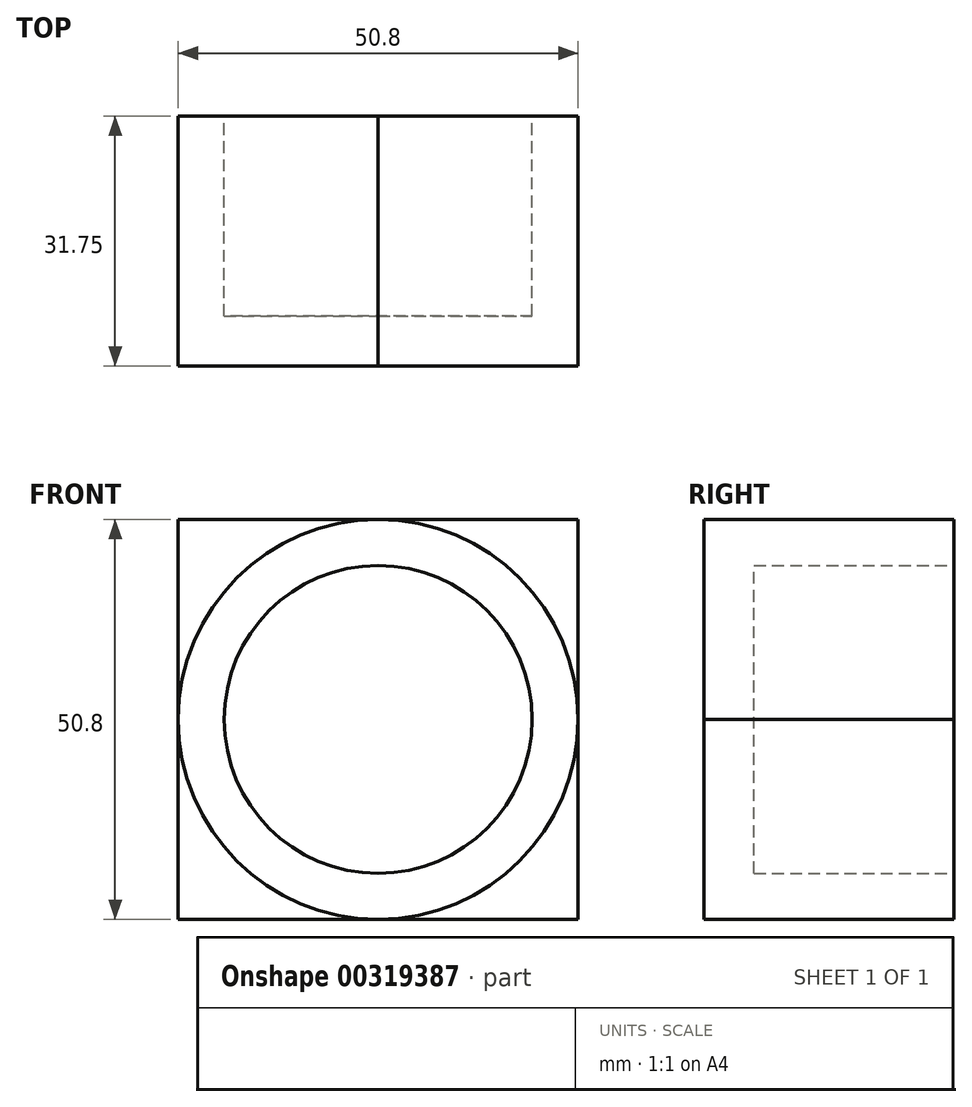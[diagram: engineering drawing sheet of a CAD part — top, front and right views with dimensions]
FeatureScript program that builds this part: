
annotation { "Feature Type Name" : "Feature", "Feature Type Description" : "" }
export const myFeature = defineFeature(function(context is Context, id is Id, definition is map)
    precondition{}
    {
        {
            var Q0;
            Q0=qCreatedBy(makeId("Front.planeOp"),FACE);
            var sketch = newSketch(context, id + "F0", { "sketchPlane" : qUnion([Q0])});
            skLineSegment(sketch, "E0.bottom", {"start": v(-25.4, 25.4) * mm, "end": v(25.4, 25.4) * mm});
            skLineSegment(sketch, "E0.top", {"start": v(-25.4, -25.4) * mm, "end": v(25.4, -25.4) * mm});
            skLineSegment(sketch, "E0.left", {"start": v(-25.4, 25.4) * mm, "end": v(-25.4, -25.4) * mm});
            skLineSegment(sketch, "E0.right", {"start": v(25.4, 25.4) * mm, "end": v(25.4, -25.4) * mm});
            skPoint(sketch, "E0.middle", {"position": v(0, 0) * mm});
            skCircle(sketch, "E1", {"center": v(0, 0) * mm, "radius": 25.4 * mm});
            skSolve(sketch);
        }
        {
            var Q0;
            {var subQ0=sQuery(id+"F0.wireOp",EDGE,"E0.left");var subQ1=sQuery(id+"F0.wireOp",EDGE,"E0.bottom");var subQ2=makeQuery(id+"F0.imprint","INTERSECT",VERTEX,{"derivedFrom":[subQ1,subQ0]});Q0=makeQuery(id+"F0.imprint","IMPRINT",FACE,{"disambiguationData":[TD([[makeQuery(id+"F0.imprint","IMPRINT",EDGE,{"disambiguationData":[TD([[subQ2,-1.0]])],"derivedFrom":subQ1}),-1.0]])]});}
            var Q1;
            {var subQ0=sQuery(id+"F0.wireOp",EDGE,"E0.right");var subQ1=sQuery(id+"F0.wireOp",EDGE,"E0.bottom");var subQ2=makeQuery(id+"F0.imprint","INTERSECT",VERTEX,{"derivedFrom":[subQ1,subQ0]});Q1=makeQuery(id+"F0.imprint","IMPRINT",FACE,{"disambiguationData":[TD([[makeQuery(id+"F0.imprint","IMPRINT",EDGE,{"disambiguationData":[TD([[subQ2,1.0]])],"derivedFrom":subQ1}),-1.0]])]});}
            var Q2;
            {var subQ0=sQuery(id+"F0.wireOp",EDGE,"E0.right");var subQ1=sQuery(id+"F0.wireOp",EDGE,"E0.top");var subQ2=makeQuery(id+"F0.imprint","INTERSECT",VERTEX,{"derivedFrom":[subQ1,subQ0]});Q2=makeQuery(id+"F0.imprint","IMPRINT",FACE,{"disambiguationData":[TD([[makeQuery(id+"F0.imprint","IMPRINT",EDGE,{"disambiguationData":[TD([[subQ2,1.0]])],"derivedFrom":subQ1}),1.0]])]});}
            var Q3;
            {var subQ0=sQuery(id+"F0.wireOp",EDGE,"E0.left");var subQ1=sQuery(id+"F0.wireOp",EDGE,"E0.top");var subQ2=makeQuery(id+"F0.imprint","INTERSECT",VERTEX,{"derivedFrom":[subQ1,subQ0]});Q3=makeQuery(id+"F0.imprint","IMPRINT",FACE,{"disambiguationData":[TD([[makeQuery(id+"F0.imprint","IMPRINT",EDGE,{"disambiguationData":[TD([[subQ2,-1.0]])],"derivedFrom":subQ1}),1.0]])]});}
            extrude(context, id + "F1", {"entities" : qUnion([Q0, Q1, Q2, Q3]), "depth" : 31.75 * mm});
        }
        {
            var Q0;
            Q0=qCreatedBy(makeId("Front.planeOp"),FACE);
            var sketch = newSketch(context, id + "F2", { "sketchPlane" : qUnion([Q0])});
            skCircle(sketch, "E2", {"center": v(0, 0) * mm, "radius": 12.7 * mm});
            skSolve(sketch);
        }
        {
            var Q0;
            Q0=makeQuery(id+"F2.imprint","IMPRINT",FACE,{"disambiguationData":[TD([[makeQuery(id+"F2.imprint","IMPRINT",EDGE,{"derivedFrom":sQuery(id+"F2.wireOp",EDGE,"E2")}),1.0]])]});
            extrude(context, id + "F3", {"entities" : qUnion([Q0]), "depth" : 25.4 * mm});
        }
        {
            var Q0;
            Q0=qCreatedBy(makeId("Front.planeOp"),FACE);
            var sketch = newSketch(context, id + "F4", { "sketchPlane" : qUnion([Q0])});
            skCircle(sketch, "E3", {"center": v(0, 0) * mm, "radius": 19.56 * mm});
            skSolve(sketch);
        }
        {
            var Q0;
            Q0=makeQuery(id+"F4.imprint","IMPRINT",FACE,{"disambiguationData":[TD([[makeQuery(id+"F4.imprint","IMPRINT",EDGE,{"derivedFrom":sQuery(id+"F4.wireOp",EDGE,"E3")}),1.0]])]});
            extrude(context, id + "F5", {"entities" : qUnion([Q0]), "operationType" : NewBodyOperationType.ADD, "depth" : 25.4 * mm});
        }
    });
